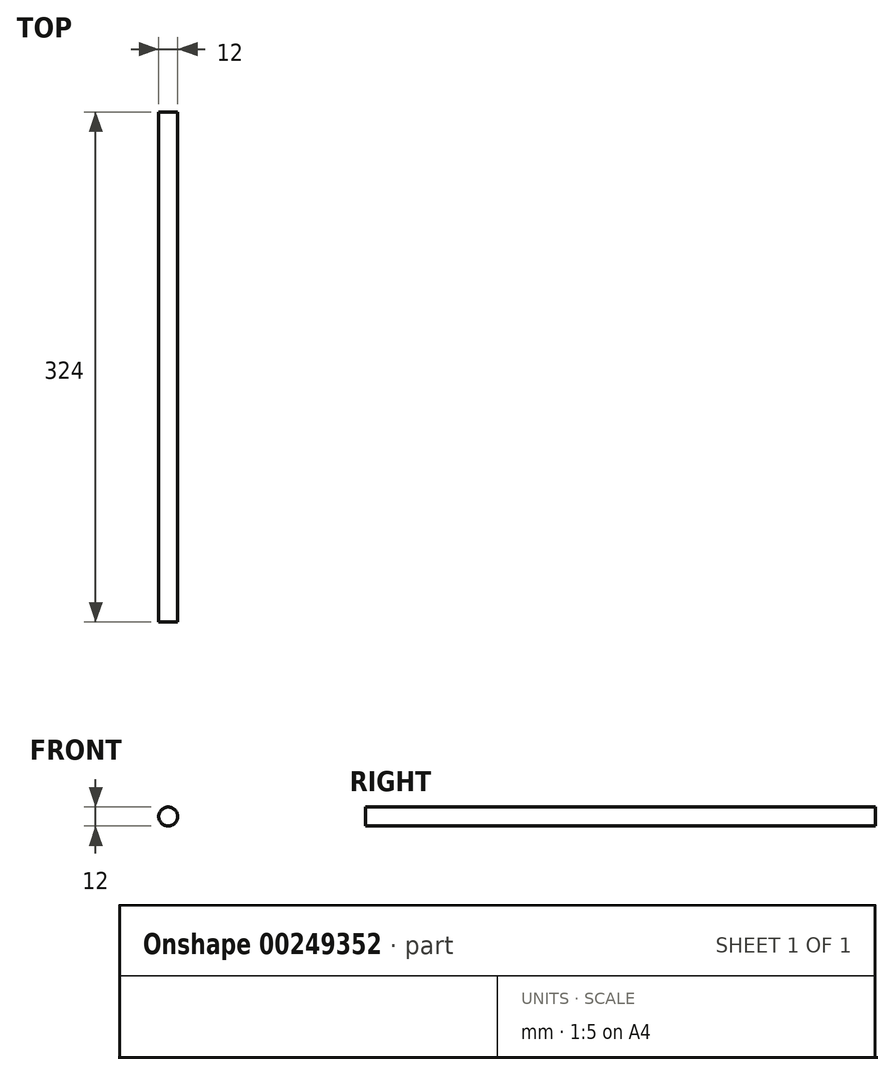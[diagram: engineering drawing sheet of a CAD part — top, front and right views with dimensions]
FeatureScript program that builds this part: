
annotation { "Feature Type Name" : "Feature", "Feature Type Description" : "" }
export const myFeature = defineFeature(function(context is Context, id is Id, definition is map)
    precondition{}
    {
        {
            var Q0;
            Q0=qCreatedBy(makeId("Front.planeOp"),FACE);
            var sketch = newSketch(context, id + "F0", { "sketchPlane" : qUnion([Q0])});
            skCircle(sketch, "E0", {"center": v(0, 0) * mm, "radius": 6 * mm});
            skSolve(sketch);
        }
        {
            var Q0;
            Q0 = qSketchRegion(id + "F0", true);
            extrude(context, id + "F1", {"entities" : qUnion([Q0]), "depth" : 324 * mm, "symmetric" : true});
        }
    });
